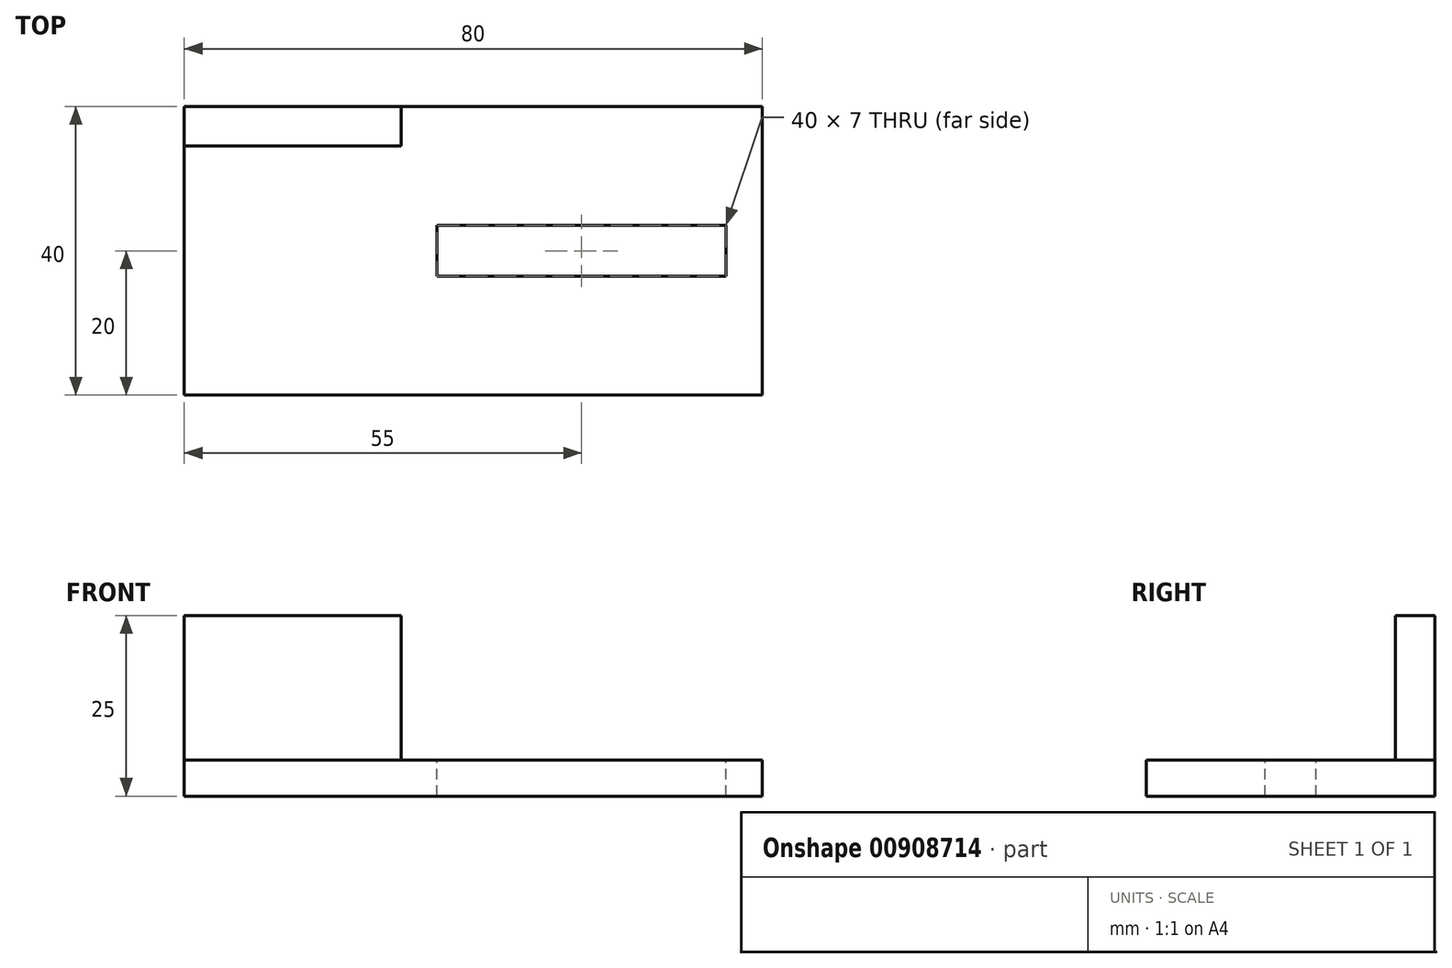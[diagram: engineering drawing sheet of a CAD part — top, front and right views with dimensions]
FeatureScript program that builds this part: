
annotation { "Feature Type Name" : "Feature", "Feature Type Description" : "" }
export const myFeature = defineFeature(function(context is Context, id is Id, definition is map)
    precondition{}
    {
        {
            var Q0;
            Q0=qCreatedBy(makeId("Top.planeOp"),FACE);
            var sketch = newSketch(context, id + "F0", { "sketchPlane" : qUnion([Q0])});
            skLineSegment(sketch, "E0.bottom", {"start": v(40, -20) * mm, "end": v(-40, -20) * mm});
            skLineSegment(sketch, "E0.top", {"start": v(40, 20) * mm, "end": v(-40, 20) * mm});
            skLineSegment(sketch, "E0.left", {"start": v(40, -20) * mm, "end": v(40, 20) * mm});
            skLineSegment(sketch, "E0.right", {"start": v(-40, -20) * mm, "end": v(-40, 20) * mm});
            skPoint(sketch, "E0.middle", {"position": v(0, 0) * mm});
            skSolve(sketch);
        }
        {
            var Q0;
            Q0=makeQuery(id+"F0.imprint","IMPRINT",FACE,{"disambiguationData":[TD([[makeQuery(id+"F0.imprint","IMPRINT",EDGE,{"derivedFrom":sQuery(id+"F0.wireOp",EDGE,"E0.bottom")}),-1.0]])]});
            extrude(context, id + "F1", {"entities" : qUnion([Q0]), "depth" : 5 * mm, "offsetDistance" : 25 * mm});
        }
        {
            var Q0;
            Q0=makeQuery(id+"F1.opExtrude","CAP_FACE",FACE,{"disambiguationData":[OSD([sQuery(id+"F0.wireOp",EDGE,"E0.bottom"),sQuery(id+"F0.wireOp",EDGE,"E0.top"),sQuery(id+"F0.wireOp",EDGE,"E0.left"),sQuery(id+"F0.wireOp",EDGE,"E0.right")])],"isStart":false});
            var sketch = newSketch(context, id + "F2", { "sketchPlane" : qUnion([Q0])});
            skLineSegment(sketch, "E1.bottom", {"start": v(-40, -14.5) * mm, "end": v(40, -14.5) * mm});
            skLineSegment(sketch, "E1.top", {"start": v(-40, 14.5) * mm, "end": v(40, 14.5) * mm});
            skLineSegment(sketch, "E1.left", {"start": v(-40, -14.5) * mm, "end": v(-40, 14.5) * mm});
            skLineSegment(sketch, "E1.right", {"start": v(40, -14.5) * mm, "end": v(40, 14.5) * mm});
            skPoint(sketch, "E1.middle", {"position": v(0, 0) * mm});
            skLineSegment(sketch, "E2.bottom", {"start": v(-40, -14.5) * mm, "end": v(-10, -14.5) * mm});
            skLineSegment(sketch, "E2.top", {"start": v(-40, -20) * mm, "end": v(-10, -20) * mm});
            skLineSegment(sketch, "E2.left", {"start": v(-40, -14.5) * mm, "end": v(-40, -20) * mm});
            skLineSegment(sketch, "E2.right", {"start": v(-10, -14.5) * mm, "end": v(-10, -20) * mm});
            skLineSegment(sketch, "E3.bottom", {"start": v(-40, 20) * mm, "end": v(-10, 20) * mm});
            skLineSegment(sketch, "E3.top", {"start": v(-40, 14.5) * mm, "end": v(-10, 14.5) * mm});
            skLineSegment(sketch, "E3.left", {"start": v(-40, 20) * mm, "end": v(-40, 14.5) * mm});
            skLineSegment(sketch, "E3.right", {"start": v(-10, 20) * mm, "end": v(-10, 14.5) * mm});
            skSolve(sketch);
        }
        {
            var Q0;
            Q0=makeQuery(id+"F2.imprint","IMPRINT",FACE,{"disambiguationData":[TD([[makeQuery(id+"F2.imprint","IMPRINT",EDGE,{"derivedFrom":sQuery(id+"F2.wireOp",EDGE,"E2.bottom")}),-1.0]])]});
            var Q1;
            Q1=makeQuery(id+"F2.imprint","IMPRINT",FACE,{"disambiguationData":[TD([[makeQuery(id+"F2.imprint","IMPRINT",EDGE,{"derivedFrom":sQuery(id+"F2.wireOp",EDGE,"E3.bottom")}),1.0]])]});
            extrude(context, id + "F3", {"entities" : qUnion([Q0, Q1]), "operationType" : NewBodyOperationType.ADD, "depth" : 20 * mm, "offsetDistance" : 25 * mm});
        }
        {
            var Q0;
            Q0=makeQuery(id+"F1.opExtrude","CAP_FACE",FACE,{"disambiguationData":[OSD([sQuery(id+"F0.wireOp",EDGE,"E0.bottom"),sQuery(id+"F0.wireOp",EDGE,"E0.top"),sQuery(id+"F0.wireOp",EDGE,"E0.left"),sQuery(id+"F0.wireOp",EDGE,"E0.right")])],"isStart":false});
            var sketch = newSketch(context, id + "F4", { "sketchPlane" : qUnion([Q0])});
            skLineSegment(sketch, "E4.bottom", {"start": v(35, -3.5) * mm, "end": v(-5, -3.5) * mm});
            skLineSegment(sketch, "E4.top", {"start": v(35, 3.5) * mm, "end": v(-5, 3.5) * mm});
            skLineSegment(sketch, "E4.left", {"start": v(35, -3.5) * mm, "end": v(35, 3.5) * mm});
            skLineSegment(sketch, "E4.right", {"start": v(-5, -3.5) * mm, "end": v(-5, 3.5) * mm});
            skPoint(sketch, "E4.middle", {"position": v(15, 0) * mm});
            skSolve(sketch);
        }
        {
            var Q0;
            Q0=makeQuery(id+"F4.imprint","IMPRINT",FACE,{"disambiguationData":[TD([[makeQuery(id+"F4.imprint","IMPRINT",EDGE,{"derivedFrom":sQuery(id+"F4.wireOp",EDGE,"E4.bottom")}),-1.0]])]});
            extrude(context, id + "F5", {"entities" : qUnion([Q0]), "operationType" : NewBodyOperationType.REMOVE, "oppositeDirection" : true, "depth" : 22.4 * mm, "offsetDistance" : 25 * mm});
        }
    });
